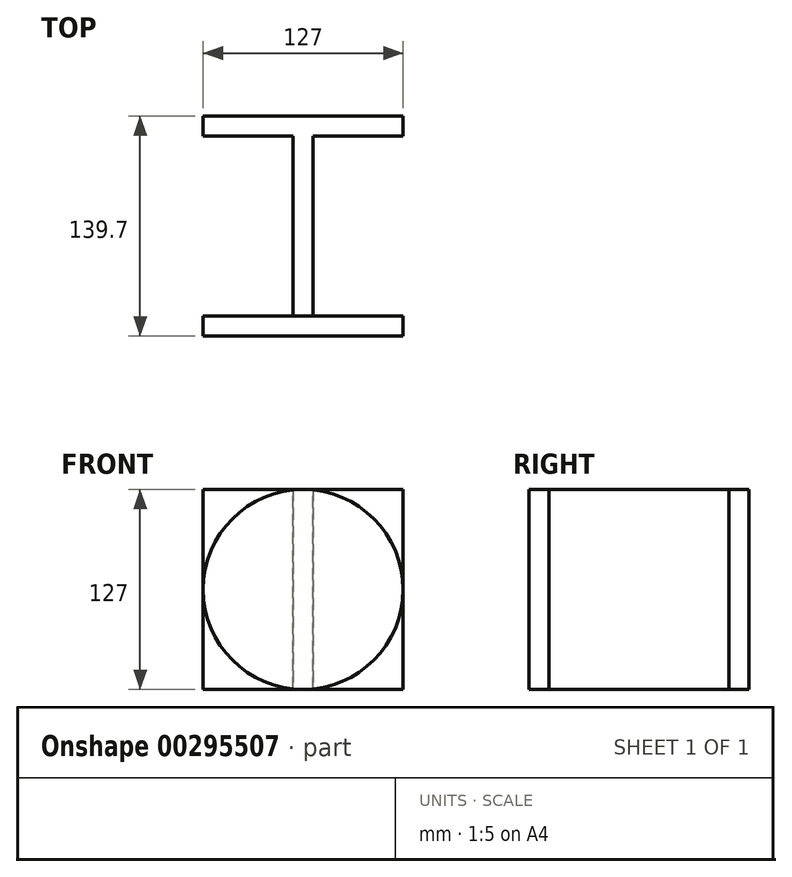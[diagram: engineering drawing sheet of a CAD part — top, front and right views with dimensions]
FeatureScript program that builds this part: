
annotation { "Feature Type Name" : "Feature", "Feature Type Description" : "" }
export const myFeature = defineFeature(function(context is Context, id is Id, definition is map)
    precondition{}
    {
        {
            var Q0;
            Q0=qCreatedBy(makeId("Front.planeOp"),FACE);
            var sketch = newSketch(context, id + "F0", { "sketchPlane" : qUnion([Q0])});
            skLineSegment(sketch, "E0.bottom", {"start": v(-63.5, 63.5) * mm, "end": v(63.5, 63.5) * mm});
            skLineSegment(sketch, "E0.top", {"start": v(-63.5, -63.5) * mm, "end": v(63.5, -63.5) * mm});
            skLineSegment(sketch, "E0.left", {"start": v(-63.5, 63.5) * mm, "end": v(-63.5, -63.5) * mm});
            skLineSegment(sketch, "E0.right", {"start": v(63.5, 63.5) * mm, "end": v(63.5, -63.5) * mm});
            skPoint(sketch, "E0.middle", {"position": v(0, 0) * mm});
            skLineSegment(sketch, "E1", {"start": v(0, 63.5) * mm, "end": v(0, -63.5) * mm});
            skLineSegment(sketch, "E2", {"start": v(-63.5, 0) * mm, "end": v(63.5, 0) * mm});
            skSolve(sketch);
        }
        {
            var Q0;
            Q0=qCreatedBy(makeId("Front.planeOp"),FACE);
            cPlane(context, id + "F1", {"entities" : qUnion([Q0]), "cplaneType" : CPlaneType.OFFSET, "offset" : 127 * mm, "width" : 152.4 * mm, "height" : 152.4 * mm});
        }
        {
            var Q0;
            Q0=qCreatedBy(id+"F1.planeOp",FACE);
            var sketch = newSketch(context, id + "F2", { "sketchPlane" : qUnion([Q0])});
            skCircle(sketch, "E3", {"center": v(0, 0) * mm, "radius": 63.5 * mm});
            skLineSegment(sketch, "E4", {"start": v(-63.5, 0) * mm, "end": v(63.5, 0) * mm});
            skLineSegment(sketch, "E5", {"start": v(0, 63.5) * mm, "end": v(0, -63.5) * mm});
            skSolve(sketch);
        }
        {
            var Q0;
            Q0=qCreatedBy(makeId("Right.planeOp"),FACE);
            var sketch = newSketch(context, id + "F3", { "sketchPlane" : qUnion([Q0])});
            skLineSegment(sketch, "E6", {"start": v(-127, 63.5) * mm, "end": v(0, 63.5) * mm});
            skLineSegment(sketch, "E7", {"start": v(-127, -63.5) * mm, "end": v(0, -63.5) * mm});
            skLineSegment(sketch, "E8", {"start": v(-127, -63.5) * mm, "end": v(-127, 63.5) * mm});
            skLineSegment(sketch, "E9", {"start": v(0, -63.5) * mm, "end": v(0, 63.5) * mm});
            skSolve(sketch);
        }
        {
            var Q0;
            Q0=makeQuery(id+"F3.imprint","IMPRINT",FACE,{"disambiguationData":[TD([[makeQuery(id+"F3.imprint","IMPRINT",EDGE,{"derivedFrom":sQuery(id+"F3.wireOp",EDGE,"E6")}),-1.0]])]});
            extrude(context, id + "F4", {"entities" : qUnion([Q0]), "endBound" : BoundingType.SYMMETRIC, "depth" : 12.7 * mm});
        }
        {
            var Q0;
            {var subQ0=sQuery(id+"F2.wireOp",EDGE,"E4");var subQ1=sQuery(id+"F2.wireOp",EDGE,"E3");var subQ2=makeQuery(id+"F2.imprint","INTERSECT",VERTEX,{"disambiguationData":[OD(0.0)],"derivedFrom":[subQ1,subQ0]});Q0=makeQuery(id+"F2.imprint","IMPRINT",FACE,{"disambiguationData":[TD([[makeQuery(id+"F2.imprint","IMPRINT",EDGE,{"disambiguationData":[TD([[subQ2,1.0]])],"derivedFrom":subQ1}),1.0]])]});}
            var Q1;
            {var subQ0=sQuery(id+"F2.wireOp",EDGE,"E4");var subQ1=sQuery(id+"F2.wireOp",EDGE,"E3");var subQ2=makeQuery(id+"F2.imprint","INTERSECT",VERTEX,{"disambiguationData":[OD(1.0)],"derivedFrom":[subQ1,subQ0]});Q1=makeQuery(id+"F2.imprint","IMPRINT",FACE,{"disambiguationData":[TD([[makeQuery(id+"F2.imprint","IMPRINT",EDGE,{"disambiguationData":[TD([[subQ2,-1.0]])],"derivedFrom":subQ1}),1.0]])]});}
            var Q2;
            {var subQ0=sQuery(id+"F2.wireOp",EDGE,"E4");var subQ1=sQuery(id+"F2.wireOp",EDGE,"E3");var subQ2=makeQuery(id+"F2.imprint","INTERSECT",VERTEX,{"disambiguationData":[OD(0.0)],"derivedFrom":[subQ1,subQ0]});Q2=makeQuery(id+"F2.imprint","IMPRINT",FACE,{"disambiguationData":[TD([[makeQuery(id+"F2.imprint","IMPRINT",EDGE,{"disambiguationData":[TD([[subQ2,-1.0]])],"derivedFrom":subQ1}),1.0]])]});}
            var Q3;
            {var subQ0=sQuery(id+"F2.wireOp",EDGE,"E4");var subQ1=sQuery(id+"F2.wireOp",EDGE,"E3");var subQ2=makeQuery(id+"F2.imprint","INTERSECT",VERTEX,{"disambiguationData":[OD(1.0)],"derivedFrom":[subQ1,subQ0]});Q3=makeQuery(id+"F2.imprint","IMPRINT",FACE,{"disambiguationData":[TD([[makeQuery(id+"F2.imprint","IMPRINT",EDGE,{"disambiguationData":[TD([[subQ2,1.0]])],"derivedFrom":subQ1}),1.0]])]});}
            extrude(context, id + "F5", {"entities" : qUnion([Q0, Q1, Q2, Q3]), "operationType" : NewBodyOperationType.ADD, "depth" : 12.7 * mm});
        }
        {
            var Q0;
            {var subQ0=sQuery(id+"F0.wireOp",EDGE,"E0.left");var subQ1=sQuery(id+"F0.wireOp",EDGE,"E0.bottom");var subQ2=makeQuery(id+"F0.imprint","INTERSECT",VERTEX,{"derivedFrom":[subQ1,subQ0]});Q0=makeQuery(id+"F0.imprint","IMPRINT",FACE,{"disambiguationData":[TD([[makeQuery(id+"F0.imprint","IMPRINT",EDGE,{"disambiguationData":[TD([[subQ2,-1.0]])],"derivedFrom":subQ1}),-1.0]])]});}
            var Q1;
            {var subQ0=sQuery(id+"F0.wireOp",EDGE,"E0.right");var subQ1=sQuery(id+"F0.wireOp",EDGE,"E0.bottom");var subQ2=makeQuery(id+"F0.imprint","INTERSECT",VERTEX,{"derivedFrom":[subQ1,subQ0]});Q1=makeQuery(id+"F0.imprint","IMPRINT",FACE,{"disambiguationData":[TD([[makeQuery(id+"F0.imprint","IMPRINT",EDGE,{"disambiguationData":[TD([[subQ2,1.0]])],"derivedFrom":subQ1}),-1.0]])]});}
            var Q2;
            {var subQ0=sQuery(id+"F0.wireOp",EDGE,"E0.right");var subQ1=sQuery(id+"F0.wireOp",EDGE,"E0.top");var subQ2=makeQuery(id+"F0.imprint","INTERSECT",VERTEX,{"derivedFrom":[subQ1,subQ0]});Q2=makeQuery(id+"F0.imprint","IMPRINT",FACE,{"disambiguationData":[TD([[makeQuery(id+"F0.imprint","IMPRINT",EDGE,{"disambiguationData":[TD([[subQ2,1.0]])],"derivedFrom":subQ1}),1.0]])]});}
            var Q3;
            {var subQ0=sQuery(id+"F0.wireOp",EDGE,"E0.left");var subQ1=sQuery(id+"F0.wireOp",EDGE,"E0.top");var subQ2=makeQuery(id+"F0.imprint","INTERSECT",VERTEX,{"derivedFrom":[subQ1,subQ0]});Q3=makeQuery(id+"F0.imprint","IMPRINT",FACE,{"disambiguationData":[TD([[makeQuery(id+"F0.imprint","IMPRINT",EDGE,{"disambiguationData":[TD([[subQ2,-1.0]])],"derivedFrom":subQ1}),1.0]])]});}
            extrude(context, id + "F6", {"entities" : qUnion([Q0, Q1, Q2, Q3]), "operationType" : NewBodyOperationType.ADD, "depth" : 12.7 * mm});
        }
    });
